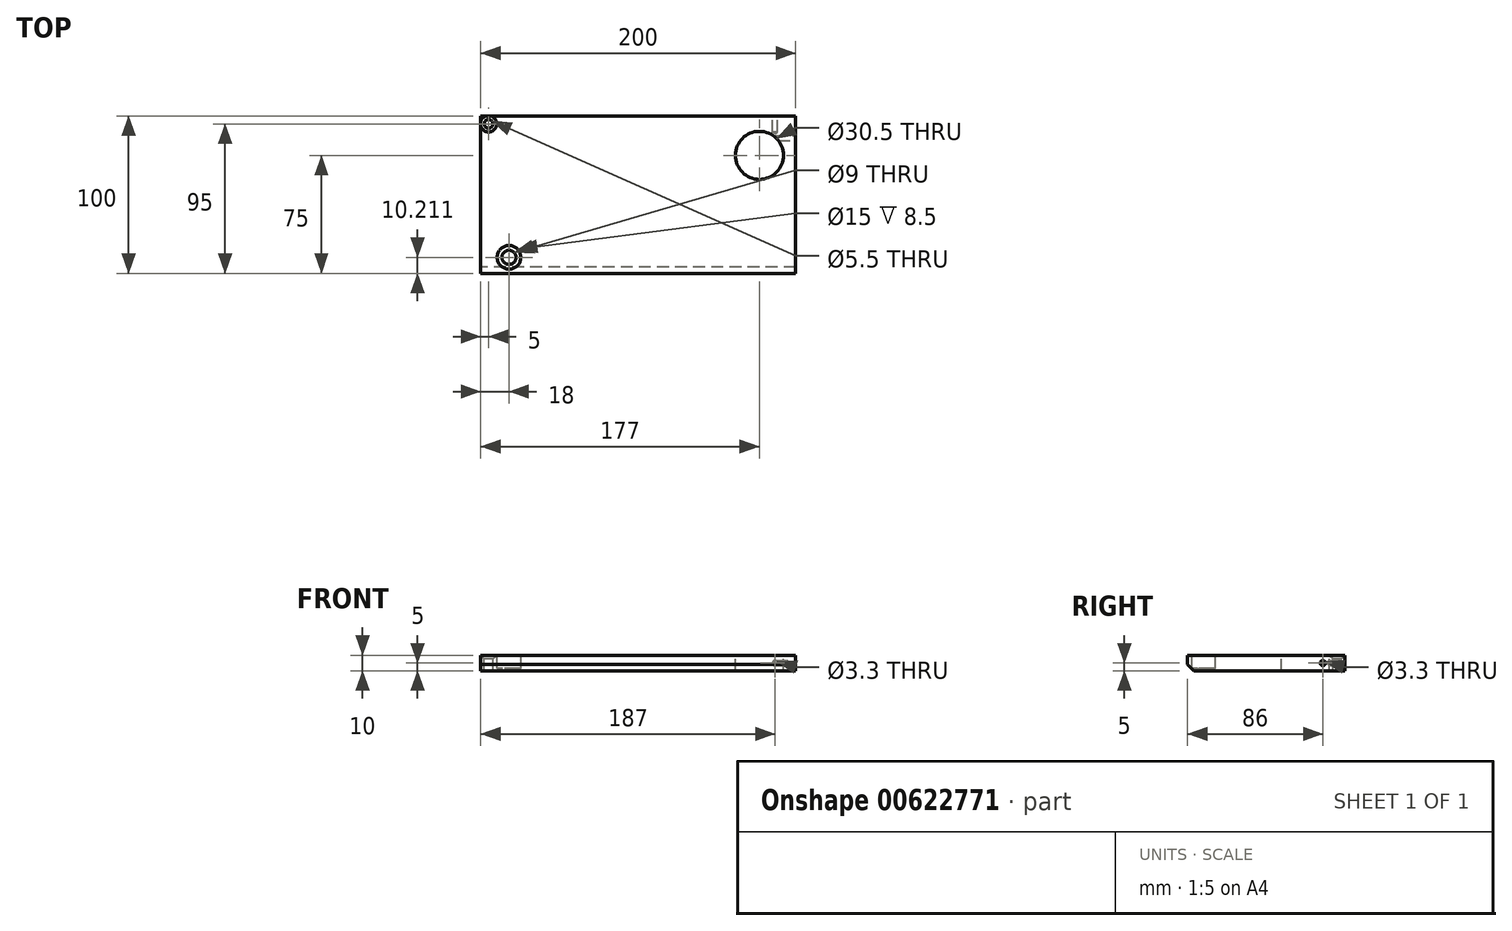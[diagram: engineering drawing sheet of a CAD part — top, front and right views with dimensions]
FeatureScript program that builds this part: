
annotation { "Feature Type Name" : "Feature", "Feature Type Description" : "" }
export const myFeature = defineFeature(function(context is Context, id is Id, definition is map)
    precondition{}
    {
        {
            var Q0;
            Q0=qCreatedBy(makeId("Top.planeOp"),FACE);
            var sketch = newSketch(context, id + "F0", { "sketchPlane" : qUnion([Q0])});
            skLineSegment(sketch, "E0.bottom", {"start": v(-100, 50) * mm, "end": v(100, 50) * mm});
            skLineSegment(sketch, "E0.top", {"start": v(-100, -50) * mm, "end": v(100, -50) * mm});
            skLineSegment(sketch, "E0.left", {"start": v(-100, 50) * mm, "end": v(-100, -50) * mm});
            skLineSegment(sketch, "E0.right", {"start": v(100, 50) * mm, "end": v(100, -50) * mm});
            skSolve(sketch);
        }
        {
            var Q0;
            Q0 = qSketchRegion(id + "F0", true);
            extrude(context, id + "F1", {"entities" : qUnion([Q0]), "depth" : 10 * mm, "offsetDistance" : 25 * mm});
        }
        {
            var Q0;
            Q0=makeQuery(id+"F1.opExtrude","CAP_EDGE",EDGE,{"disambiguationData":[OSD([sQuery(id+"F0.wireOp",EDGE,"E0.top")])],"isStart":true});
            chamfer(context, id + "F2", {"entities" : qUnion([Q0]), "width" : 4 * mm, "tangentPropagation" : true});
        }
        {
            var Q0;
            Q0=makeQuery(id+"F1.opExtrude","CAP_FACE",FACE,{"disambiguationData":[OSD([sQuery(id+"F0.wireOp",EDGE,"E0.bottom"),sQuery(id+"F0.wireOp",EDGE,"E0.top"),sQuery(id+"F0.wireOp",EDGE,"E0.left"),sQuery(id+"F0.wireOp",EDGE,"E0.right")])],"isStart":false});
            var sketch = newSketch(context, id + "F3", { "sketchPlane" : qUnion([Q0])});
            skPoint(sketch, "E1", {"position": v(-82, -39.79) * mm});
            skSolve(sketch);
        }
        {
            var Q0;
            Q0=sQuery(id+"F3.wireOp",VERTEX,"E1");
            var Q1;
            Q1=makeQuery(id+"F1.opExtrude","SWEPT_BODY",BODY,{"disambiguationData":[OSD([sQuery(id+"F0.wireOp",EDGE,"E0.bottom"),sQuery(id+"F0.wireOp",EDGE,"E0.top"),sQuery(id+"F0.wireOp",EDGE,"E0.left"),sQuery(id+"F0.wireOp",EDGE,"E0.right")])]});
            hole(context, id + "F4", {"style" : HoleStyle.C_BORE, "endStyle" : HoleEndStyle.BLIND, "holeDiameter" : 9 * mm, "cBoreDiameter" : 15 * mm, "cBoreDepth" : 8.5 * mm, "majorDiameter" : 5 * mm, "holeDepth" : 10 * mm, "isTappedThrough" : true, "tappedDepth" : 12 * mm, "tapClearance" : 3, "locations" : qUnion([Q0]), "scope" : qUnion([Q1])});
        }
        {
            var Q0;
            Q0=makeQuery(id+"F1.opExtrude","CAP_FACE",FACE,{"disambiguationData":[OSD([sQuery(id+"F0.wireOp",EDGE,"E0.bottom"),sQuery(id+"F0.wireOp",EDGE,"E0.top"),sQuery(id+"F0.wireOp",EDGE,"E0.left"),sQuery(id+"F0.wireOp",EDGE,"E0.right")])],"isStart":false});
            var sketch = newSketch(context, id + "F5", { "sketchPlane" : qUnion([Q0])});
            skPoint(sketch, "E2", {"position": v(-95, 45) * mm});
            skSolve(sketch);
        }
        {
            var Q0;
            Q0=sQuery(id+"F5.wireOp",VERTEX,"E2");
            var Q1;
            Q1=makeQuery(id+"F1.opExtrude","SWEPT_BODY",BODY,{"disambiguationData":[OSD([sQuery(id+"F0.wireOp",EDGE,"E0.bottom"),sQuery(id+"F0.wireOp",EDGE,"E0.top"),sQuery(id+"F0.wireOp",EDGE,"E0.left"),sQuery(id+"F0.wireOp",EDGE,"E0.right")])]});
            hole(context, id + "F6", {"style" : HoleStyle.C_SINK, "endStyle" : HoleEndStyle.BLIND, "holeDiameter" : 5.5 * mm, "cSinkDiameter" : 10.4 * mm, "cSinkAngle" : 90 * degree, "majorDiameter" : 5 * mm, "holeDepth" : 10 * mm, "isTappedThrough" : true, "tappedDepth" : 12 * mm, "tapClearance" : 3, "locations" : qUnion([Q0]), "scope" : qUnion([Q1])});
        }
        {
            var Q0;
            {var subQ0=sQuery(id+"F0.wireOp",EDGE,"E0.left");var subQ1=sQuery(id+"F0.wireOp",EDGE,"E0.top");var subQ2=sQuery(id+"F0.wireOp",EDGE,"E0.right");var subQ3=sQuery(id+"F0.wireOp",EDGE,"E0.bottom");Q0=makeQuery(id+"F6.hole-0.boolean.opBoolean","SPLIT",FACE,{"disambiguationData":[TD([makeQuery(id+"F1.opExtrude","SWEPT_FACE",FACE,{"disambiguationData":[OSD([subQ3])]}),makeQuery(id+"F1.opExtrude","SWEPT_FACE",FACE,{"disambiguationData":[OSD([subQ1])]}),makeQuery(id+"F1.opExtrude","SWEPT_FACE",FACE,{"disambiguationData":[OSD([subQ0])]}),makeQuery(id+"F1.opExtrude","SWEPT_FACE",FACE,{"disambiguationData":[OSD([subQ2])]}),makeQuery(id+"F4.hole-0.boolean.opBoolean","COPY",FACE,{"derivedFrom":makeQuery(id+"F4.hole-0.opRevolve","SWEPT_FACE",FACE,{"disambiguationData":[OSD([sQuery(id+"F4.hole-0.sketch.wireOp",EDGE,"cbore_start_line_2")])]})}),makeQuery(id+"F6.hole-0.opRevolve","SWEPT_FACE",FACE,{"disambiguationData":[OSD([sQuery(id+"F6.hole-0.sketch.wireOp",EDGE,"csink_start_line_1")])]})])],"derivedFrom":makeQuery(id+"F1.opExtrude","CAP_FACE",FACE,{"disambiguationData":[OSD([subQ3,subQ1,subQ0,subQ2])],"isStart":false})});}
            var sketch = newSketch(context, id + "F7", { "sketchPlane" : qUnion([Q0])});
            skPoint(sketch, "E3", {"position": v(77, 25) * mm});
            skSolve(sketch);
        }
        {
            var Q0;
            Q0=sQuery(id+"F7.wireOp",VERTEX,"E3");
            var Q1;
            Q1=makeQuery(id+"F1.opExtrude","SWEPT_BODY",BODY,{"disambiguationData":[OSD([sQuery(id+"F0.wireOp",EDGE,"E0.bottom"),sQuery(id+"F0.wireOp",EDGE,"E0.top"),sQuery(id+"F0.wireOp",EDGE,"E0.left"),sQuery(id+"F0.wireOp",EDGE,"E0.right")])]});
            hole(context, id + "F8", {"style" : HoleStyle.SIMPLE, "endStyle" : HoleEndStyle.BLIND, "holeDiameter" : 30.5 * mm, "majorDiameter" : 5 * mm, "holeDepth" : 10 * mm, "isTappedThrough" : true, "tappedDepth" : 12 * mm, "tapClearance" : 3, "locations" : qUnion([Q0]), "scope" : qUnion([Q1])});
        }
        {
            var Q0;
            Q0=makeQuery(id+"F1.opExtrude","SWEPT_FACE",FACE,{"disambiguationData":[OSD([sQuery(id+"F0.wireOp",EDGE,"E0.right")])]});
            var sketch = newSketch(context, id + "F9", { "sketchPlane" : qUnion([Q0])});
            skPoint(sketch, "E4", {"position": v(36, 5) * mm});
            skSolve(sketch);
        }
        {
            var Q0;
            Q0=sQuery(id+"F9.wireOp",VERTEX,"E4");
            var Q1;
            Q1=makeQuery(id+"F1.opExtrude","SWEPT_BODY",BODY,{"disambiguationData":[OSD([sQuery(id+"F0.wireOp",EDGE,"E0.bottom"),sQuery(id+"F0.wireOp",EDGE,"E0.top"),sQuery(id+"F0.wireOp",EDGE,"E0.left"),sQuery(id+"F0.wireOp",EDGE,"E0.right")])]});
            hole(context, id + "F10", {"style" : HoleStyle.SIMPLE, "endStyle" : HoleEndStyle.BLIND, "standardTappedOrClearance" : lookupTablePath({ "standard" : "ISO", "engagement" : "75%", "pitch" : "0.7 mm", "size" : "M4", "type" : "Tapped" }), "standardBlindInLast" : lookupTablePath({ "standard" : "ISO", "engagement" : "75%", "pitch" : "0.7 mm", "size" : "M4", "type" : "Tapped" }), "holeDiameter" : 3.3 * mm, "majorDiameter" : 4 * mm, "showTappedDepth" : true, "holeDepth" : 13.6 * mm, "isTappedThrough" : true, "tappedDepth" : 11.5 * mm, "tapClearance" : 3, "locations" : qUnion([Q0]), "scope" : qUnion([Q1])});
        }
        {
            var Q0;
            Q0=makeQuery(id+"F1.opExtrude","SWEPT_FACE",FACE,{"disambiguationData":[OSD([sQuery(id+"F0.wireOp",EDGE,"E0.bottom")])]});
            var sketch = newSketch(context, id + "F11", { "sketchPlane" : qUnion([Q0])});
            skPoint(sketch, "E5", {"position": v(-87, 5) * mm});
            skSolve(sketch);
        }
        {
            var Q0;
            Q0=sQuery(id+"F11.wireOp",VERTEX,"E5");
            var Q1;
            Q1=makeQuery(id+"F1.opExtrude","SWEPT_BODY",BODY,{"disambiguationData":[OSD([sQuery(id+"F0.wireOp",EDGE,"E0.bottom"),sQuery(id+"F0.wireOp",EDGE,"E0.top"),sQuery(id+"F0.wireOp",EDGE,"E0.left"),sQuery(id+"F0.wireOp",EDGE,"E0.right")])]});
            hole(context, id + "F12", {"style" : HoleStyle.SIMPLE, "endStyle" : HoleEndStyle.BLIND, "standardTappedOrClearance" : lookupTablePath({ "standard" : "ISO", "engagement" : "75%", "pitch" : "0.7 mm", "size" : "M4", "type" : "Tapped" }), "standardBlindInLast" : lookupTablePath({ "standard" : "ISO", "engagement" : "75%", "pitch" : "0.7 mm", "size" : "M4", "type" : "Tapped" }), "holeDiameter" : 3.3 * mm, "majorDiameter" : 4 * mm, "showTappedDepth" : true, "holeDepth" : 10.1 * mm, "isTappedThrough" : true, "tappedDepth" : 8 * mm, "tapClearance" : 3, "locations" : qUnion([Q0]), "scope" : qUnion([Q1])});
        }
    });
